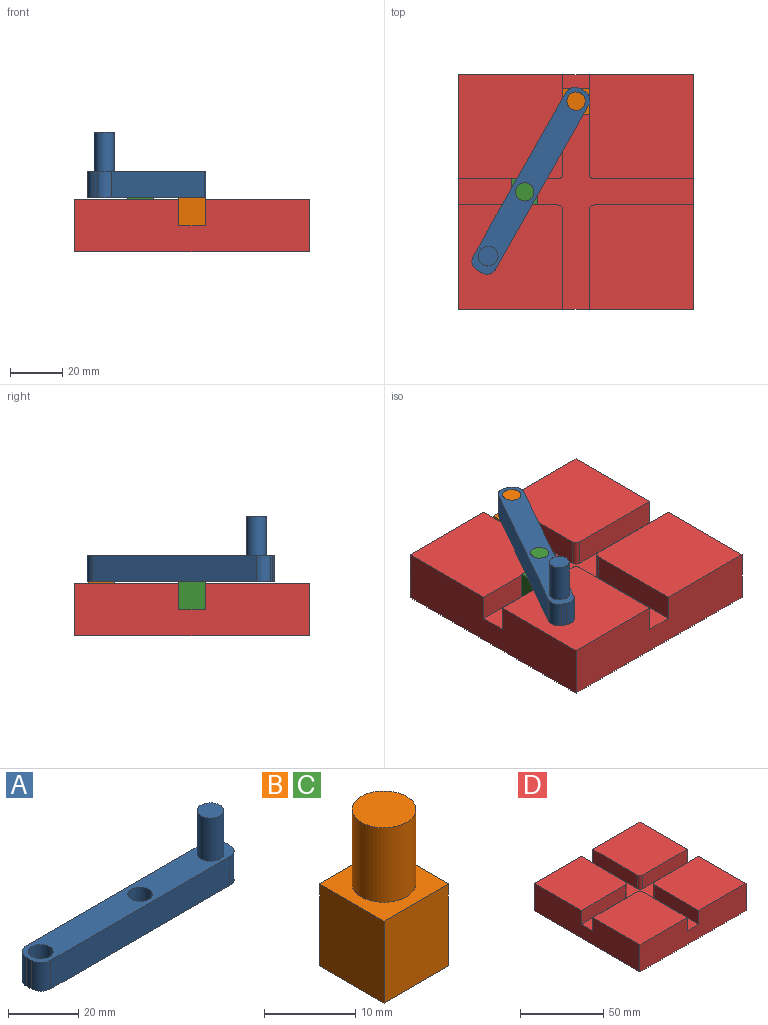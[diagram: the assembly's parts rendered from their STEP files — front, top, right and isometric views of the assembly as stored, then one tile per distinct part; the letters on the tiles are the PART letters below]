
ASSEMBLY  parts=4 mates=4
PART A: 14 faces, bbox 80x10x25 mm
  f0: plane 10x2mm, normal (-1,0,0), area 20mm2, adj f6,f7,f10,f13
  f1: plane 72x10mm, normal (0,-1,0), area 720mm2, adj f6,f7,f10,f11
  f2: plane 10x2mm, normal (1,0,0), area 20mm2, adj f6,f7,f11,f12
  f3: cylinder r=3.5mm len=10mm, axis (0,0,-1), area 219.9mm2, adj f6,f7
  f4: cylinder r=3.5mm len=10mm, axis (0,0,-1), area 219.9mm2, adj f6,f7
  f5: plane 72x10mm, normal (0,1,0), area 720mm2, adj f6,f7,f12,f13
  f6: plane 80x10mm, normal (0,0,1), area 664.4mm2, adj f0,f1,f2,f3,f4,f5,f8,f10
  f7: plane 80x10mm, normal (0,0,-1), area 709.3mm2, adj f0,f1,f2,f3,f4,f5,f10,f11
  f8: cylinder r=3.78mm len=15mm, axis (0,0,-1), area 356.2mm2, adj f6,f9
  f9: plane 7.56x7.56mm, normal (0,0,1), area 44.9mm2, adj f8
  f10: cylinder r=4mm len=10mm, axis (0,0,1), area 62.8mm2, adj f0,f1,f6,f7
  f11: cylinder r=4mm len=10mm, axis (0,0,-1), area 62.8mm2, adj f1,f2,f6,f7
  f12: cylinder r=4mm len=10mm, axis (0,0,1), area 62.8mm2, adj f2,f5,f6,f7
  f13: cylinder r=4mm len=10mm, axis (0,0,-1), area 62.8mm2, adj f0,f5,f6,f7
PART B: 8 faces, bbox 10x10x21 mm
  f0: plane 11x10mm, normal (0,1,0), area 110mm2, adj f1,f3,f4,f5
  f1: plane 11x10mm, normal (-1,0,0), area 110mm2, adj f0,f2,f4,f5
  f2: plane 11x10mm, normal (0,-1,0), area 110mm2, adj f1,f3,f4,f5
  f3: plane 11x10mm, normal (1,0,0), area 110mm2, adj f0,f2,f4,f5
  f4: plane 10x10mm, normal (0,0,1), area 61.5mm2, adj f0,f1,f2,f3,f6
  f5: plane 10x10mm, normal (0,0,-1), area 100mm2, adj f0,f1,f2,f3
  f6: cylinder r=3.5mm len=10mm, axis (0,0,-1), area 219.9mm2, adj f4,f7
  f7: plane 7x7mm, normal (0,0,1), area 38.5mm2, adj f6
PART C: same geometry as B
PART D: 22 faces, bbox 90x90x20 mm
  f0: plane 40x40mm, normal (0,0,1), area 1599.1mm2, adj f5,f6,f11,f12,f21
  f1: plane 40x40mm, normal (0,0,1), area 1599.1mm2, adj f4,f6,f13,f14,f20
  f2: plane 40x40mm, normal (0,0,1), area 1599.1mm2, adj f3,f5,f9,f10,f19
  f3: plane 90x20mm, normal (-1,0,0), area 1700mm2, adj f2,f4,f5,f7,f8,f9,f16,f17
  f4: plane 90x20mm, normal (0,1,0), area 1700mm2, adj f1,f3,f6,f7,f8,f14,f15,f17
  f5: plane 90x20mm, normal (0,-1,0), area 1700mm2, adj f0,f2,f3,f6,f8,f10,f11,f17
  f6: plane 90x20mm, normal (1,0,0), area 1700mm2, adj f0,f1,f4,f5,f8,f12,f13,f17
  f7: plane 40x40mm, normal (0,0,1), area 1599.1mm2, adj f3,f4,f15,f16,f18
  f8: plane 90x90mm, normal (0,0,-1), area 8100mm2, adj f3,f4,f5,f6
  f9: plane 38x10mm, normal (0,1,0), area 380mm2, adj f2,f3,f17,f19
  f10: plane 38x10mm, normal (1,0,0), area 380mm2, adj f2,f5,f17,f19
  f11: plane 38x10mm, normal (-1,0,0), area 380mm2, adj f0,f5,f17,f21
  f12: plane 38x10mm, normal (0,1,0), area 380mm2, adj f0,f6,f17,f21
  f13: plane 38x10mm, normal (0,-1,0), area 380mm2, adj f1,f6,f17,f20
  f14: plane 38x10mm, normal (-1,0,0), area 380mm2, adj f1,f4,f17,f20
  f15: plane 38x10mm, normal (1,0,0), area 380mm2, adj f4,f7,f17,f18
  f16: plane 38x10mm, normal (0,-1,0), area 380mm2, adj f3,f7,f17,f18
  f17: plane 90x90mm, normal (0,0,1), area 1703.4mm2, adj f3,f4,f5,f6,f9,f10,f11,f12
  f18: cylinder r=2mm len=10mm, axis (0,0,-1), area 31.4mm2, adj f7,f15,f16,f17
  f19: cylinder r=2mm len=10mm, axis (0,0,1), area 31.4mm2, adj f2,f9,f10,f17
  f20: cylinder r=2mm len=10mm, axis (0,0,1), area 31.4mm2, adj f1,f13,f14,f17
  f21: cylinder r=2mm len=10mm, axis (0,0,-1), area 31.4mm2, adj f0,f11,f12,f17
PLACE A rot(axis=(0,0,-1),119.5deg) t=(-18.89,11.41,20.71)mm
PLACE B t=(-45,119.8,-0.29)mm
PLACE C t=(-64.72,85,-0.29)mm
PLACE D t=(-45,45,0)mm
MATE revolute A.f3 <-> C.f6  axis (0,0,1) through (-64.72,45,30.71)mm
MATE slider D.f3 <-> C.f1  axis (-1,0,0) through (-90,45,9.71)mm
MATE slider D.f5 <-> B.f2  axis (0,-1,0) through (-45,0,9.71)mm
MATE revolute B.f6 <-> A.f4  axis (0,0,1) through (-45,79.8,30.71)mm
